# Revit family: GRIFO DUCHA KILY con accesorios de ducha
name_source: partatom
category: Aparatos sanitarios
revit_build: Autodesk Revit 2015 (Build: 20140223_1515(x64)
units: mm (PartAtom-declared; Revit-internal decimal feet)

## types (1)
- 4953000
    Accionamiento = Por maneta
    CAUDAL = 25,2 l/min a 3 bar
    Comentarios de tipo = ◦Grifo monomando ducha
◦Acabado Cromo
◦Aireador oculto
◦Sin accesorios de ducha
◦Cartucho con discos cerámicos de diámetro 35 mm
◦Entrada Hembra 3/4" a 1/2'' con excéntrica y embellecedor
    Conexión AC = Sí
    Conexión AF = Sí
    Código de montaje = C1030220
    Descripción = Grifo monomando de ducha Kily. Colección de líneas refinadas y elegantes que se adaptan a todo tipo de ambientes. Su original maneta de forma ondulada destaca en inclinación del escultural diseño del cuerpo del grifo. Una grifería que decora el espacio de baño con personalidad siendo piezas prácticas y ergonómicas muy confortables con el toque de distinción perfecto.
    ENTRADA = Entrada Hembra 3/4" a 1/2'' con excéntrica y embellecedor.
    Elevación por defecto = 1219 mm
    Fabricante = PRESTO IBÉRICA
    Imagen de tipo = <Ninguno>
    Material = LATON CROMADO
    Modelo = KILY
    REFERENCIA = 4953000
    TIPO DE AGUA = Fria/Caliente
    Teléfono = (+34) 915 782 575
    URL = http://www.griferiasgalindo.com
